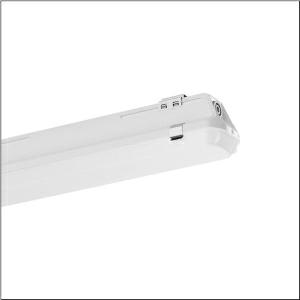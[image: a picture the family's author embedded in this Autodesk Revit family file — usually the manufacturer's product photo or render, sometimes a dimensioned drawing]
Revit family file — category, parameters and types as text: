
# Revit family: monsun_r__21_51fb107p460b005_4f74
name_source: partatom
category: Lighting Fixtures
units: mm (PartAtom-declared; Revit-internal decimal feet)

## family parameters
Cut with Voids When Loaded = No
Host = Face
Light Source = No
Part Type = Normal
Room Calculation Point = No
Round Connector Dimension = Use Diameter
Shared = No

## types (1)
- Monsun® 21 (1 x LED, 6000 lm, 38 W, 4000K)
    Apparent Load = 38 VA
    CIE Flux Codes = 47 77 93 94 100
    Color Rendering = 80
    Color Temperature = 4000K
    Default Elevation = 1800 mm
    Description = Monsun® 21, damp-proof luminaire, chain hanger, primary optical cover: enclosure, of PMMA, light emission: direct distribution, primary light characteristic: symmetric, installation type: suspended mounting, surface-mounted, horizontal mounting, vertical mounting, LED, rated luminous flux: 6.000lm, luminous efficacy: 158lm/W, light colour: 840, colour temperature: 4000K, control gear: ECG, with terminal, 3-pole, max. 2.5mm², through-wiring: 5x 2.5mm², mains connection: 220..240V, AC, 50/60Hz, rated input power: 38W, housing, of glass-fibre reinforced polyester, uncoated, bright grey, incl. chain hanger, length: 1.590mm, width: 90mm, height: 88mm, clip for enclosure, of stainless steel (V2A), ceiling mounting element, of stainless steel (V2A), chain hanger, of stainless steel (V2A), protection rating (complete): IP66, insulation class (complete): insulation class I (protective earthing), certification: CE, ENEC, VDE, UKCA, protection symbol: D, impact resistance: IK04, permissible operating ambient temperature: -25..+35°C, standard: EN 50419, EN 60598-2-1, corresponds to IFS (International Featured Standards) requirements for safety and quality in the food industry, for indoor or canopied outdoor use, no direct snow, no direct sun, no direct rain, contact your sales advisor before using the luminaires in applications with unclear chemical exposure, large temperature fluctuations or condensation-forming humidity, LABS conformity tested according to VDMA 24364:2018-05, packaging unit: 1 piece
    Height = 89 mm
    Lamp = 1 x LED
    Lamp Light Flux = 6000 lm
    Lamp Power = 38 W
    Lamp count = 1
    Length = 1590 mm
    Luminous efficacy = 158 lm/W
    Manufacturer = Siteco
    ModVariant = No
    Model = 51FB107P460B005
    Mounting Place = Ceiling
    Mounting Type = Surface mounted
    Number of Poles = 1
    OnlyDefault = Yes
    Power Factor = 1
    Product Name = Monsun® 21
    Product group = damp-proof luminaire
    ProductGroupID = 300
    Protection Class = Protection class I
    Protection Degree = IP 66
    RLX_Detail_Level = 1
    RLX_Emergency_Light_Flux = 0 lm
    RLX_Emergency_Type = 0
    RLX_Emergency_Type_DB = No
    RlxData = <blob elided: 88269 chars, md5=02c39795>
    Socket = socket
    Standby Power = 0 W
    System Light Flux = 6000 lm
    System Power = 38 W
    Type Comments = Product without accessories
    Type Image = l_1319656.jpg
    URL = http://relux.com
    VarID = ---
    Voltage = 0 V
    Weight = 0.00 kg
    Width = 90 mm

## geometry (parser evidence)
native form markers: Blend x4, Sweep x14
no freeform markers — native parametric forms only
